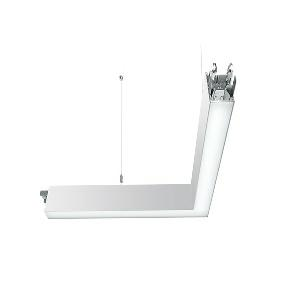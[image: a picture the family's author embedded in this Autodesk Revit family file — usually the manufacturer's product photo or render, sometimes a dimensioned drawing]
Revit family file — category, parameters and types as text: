
# Revit family: idoo_line_-_ilp_3000_840_d_ll_mid_00807700_d295
name_source: partatom
category: Lighting Fixtures
units: mm (PartAtom-declared; Revit-internal decimal feet)

## family parameters
Cut with Voids When Loaded = No
Host = Face
Light Source = No
Part Type = Normal
Room Calculation Point = No
Round Connector Dimension = Use Diameter
Shared = No

## types (1)
- IDOO.line - ILP 3000/840/D/LL MID (1 x LED, 3150 lm, 4000K)
    Apparent Load = 23 VA
    Approval mark = CE
    CIE Flux Codes = 66 91 98 40 100
    Color Rendering = 80-89
    Color Temperature = 4000K
    Control Gear = Electronic ballast
    Default Elevation = 1800 mm
    Description = ILP 3000/840/D|Suspended luminaire|light source: LED|connected load: 220-240 V, 50/60 Hz|Power consumption: approx. 23 W|standby: approx. 0,20|luminous flux: 3150 lm|luminous efficacy: 136 lm/W|light distribution: Direct/indirect|direct ratio: approx. 40 %|colour temperature: Cold white, ca. 4000 K|color rendering index (CRI): >= 80|chromaticity tolerance:  3 SDCM|System of protection: IP 40|technology: Continuously dimmable|luminaire body|material: Sectional aluminium|colour: White|lamp cover: Acrylic (PMMA), Clear|Fastening: Steel cable 0.3 - 0.7 m|glare control: Prism aperture|luminance(L65): <= 2700 cd/m|unified glare rating(4H 8H): <=  16|special features: DALI Load 1x, TouchDIM - dimming via standard switch, Through-wired, up to 18 m on one mains connection, Flicker-free, Continous light without dark z, 90░ rerouting on the left side, Suitable as emergency lighting, Mechanical and electrical connection of the individual modules without tools|
    Frequency = 50 Hz
    Height = 110 mm
    Lamp = 1 x LED
    Lamp Light Flux = 3150 lm
    Lamp count = 1
    Length = 600 mm
    Luminous efficacy = 137 lm/W
    Manufacturer = Waldmann
    ModVariant = No
    Model = 00807700
    Mounting Place = Ceiling
    Mounting Type = Pendant
    Number of Poles = 1
    OnlyDefault = Yes
    Power Factor = 1
    Product Name = IDOO.line - ILP 3000/840/D/LL MID
    Product group = Suspended luminaire
    ProductGroupID = 9
    Protection Class = Protection class I
    Protection Degree = IP 40
    RLX_Detail_Level = 1
    RLX_Emergency_Light_Flux = 0 lm
    RLX_Emergency_Type = 0
    RLX_Emergency_Type_DB = No
    RlxData = <blob elided: 20905 chars, md5=4602e532>
    Socket = socket
    Standby Power = 0 W
    System Light Flux = 3150 lm
    System Power = 23 W
    Type Comments = Product without accessories
    Type Image = ilp_dlp_ll_ws.jpg
    URL = http://relux.com
    VarID = ---
    Voltage = 230 V
    Voltage Range = 220-240 V
    Weight = 0.00 kg
    Width = 600 mm

## geometry (parser evidence)
native form markers: Blend x4, Sweep x14
no freeform markers — native parametric forms only
